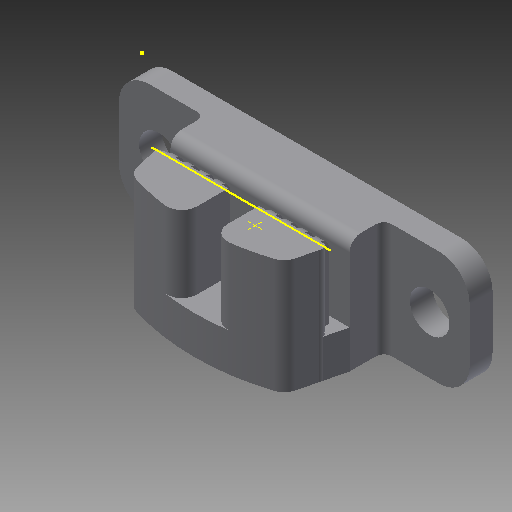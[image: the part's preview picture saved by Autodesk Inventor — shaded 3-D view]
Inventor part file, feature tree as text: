
AUTODESK INVENTOR PART (.ipt)
format: ipt  version: 2018 (Build 220112000, 112)  size: 601,600 bytes
history: native  units: mm
features: sketch x13, extrude x10, projected_geometry x10, fillet x2, direct_edit x1, move_body x1
ambient origin geometry x8: Origin, YZ Plane, XZ Plane, XY Plane, X Axis, Y Axis, Z Axis, Center Point
bodies: Solid1 (feature_tree)
feature tree (37):
  extrude  "Extrusion1"  Depth=15.0mm
  extrude  "Extrusion2"  Depth=15.0mm TaperAngle=0.0deg
  sketch  "Sketch3"  dims[d10=7.25mm d11=90.0deg]
  sketch  "Sketch4"  dims[d12=12.0mm d13=0.0mm d14=10.0mm]
  extrude  "Extrusion3"  TaperAngle=90.0deg  [1 undecoded]
  extrude  "Extrusion4"  Depth=10.0mm
  sketch  "Sketch6"  dims[d21=1.0mm d22=1.2mm d23=1.0mm d24=1.0mm d25=1.0mm d26=1.0mm d27=1.2mm d28=1.0mm d29=1.0mm]
  extrude  "Extrusion5"  Depth=1.0mm
  extrude  "Extrusion6"  Depth=0.75mm
  extrude  "Extrusion7"  Depth=15.0mm TaperAngle=0.0deg
  extrude  "Extrusion8"  Depth=10.0mm TaperAngle=0.0deg
  fillet  "Fillet1"  Radius=10.0mm
  extrude  "Extrusion9"  Depth=1.5mm
  extrude  "Extrusion10"  Depth=1.0mm
  fillet  "Fillet2"  Radius=7.0mm
  sketch  "Sketch13"  dims[d70=2.75mm d71=0.0mm d72=90.0deg d73=90.0deg d74=10.0mm d75=0.0mm d76=2.0mm d77=0.0mm d78=0.0mm d79=-2.5mm]
  direct_edit  "Direct Edit1"
  sketch  "Sketch1"  dims[d0=46.0mm d1=15.0mm]
  sketch  "Sketch2"  dims[d6=4.0mm d7=15.0mm d8=0.0mm]
  projected_geometry  "Projected Loop1"
  sketch  "Sketch5"  dims[d20=1.0mm]
  projected_geometry  "Projected Loop2"
  projected_geometry  "Projected Loop3"
  projected_geometry  "Projected Loop4"
  sketch  "Sketch7"  dims[d34=1.0mm d35=1.0mm d36=1.0mm d37=1.2mm d38=1.0mm d39=1.0mm d40=1.0mm d41=1.0mm d42=1.2mm d43=1.0mm d52=0.75mm]
  projected_geometry  "Projected Loop5"
  projected_geometry  "Projected Loop6"
  sketch  "Sketch8"  dims[d53=2.0mm d54=0.0mm d55=15.0mm d56=0.0mm]
  projected_geometry  "Projected Loop7"
  projected_geometry  "Projected Loop8"
  sketch  "Sketch9"  dims[d57=0.9mm d58=10.0mm d59=0.0mm d60=10.0mm d61=0.0mm]
  projected_geometry  "Projected Loop9"
  sketch  "Sketch10"  dims[d62=10.0mm d63=0.0mm d64=1.5mm]
  sketch  "Sketch11"  dims[d65=10.0mm d66=0.0mm d67=1.0mm d68=7.0mm]
  sketch  "Sketch12"  dims[d69=2.0mm]
  projected_geometry  "Projected Loop10"
  move_body  "Move1"
note: 1 required parameter value undecoded (feature->parameter linkage not recoverable at this tier; creation-order binding heuristic only, values carry confidence <= 0.55)
